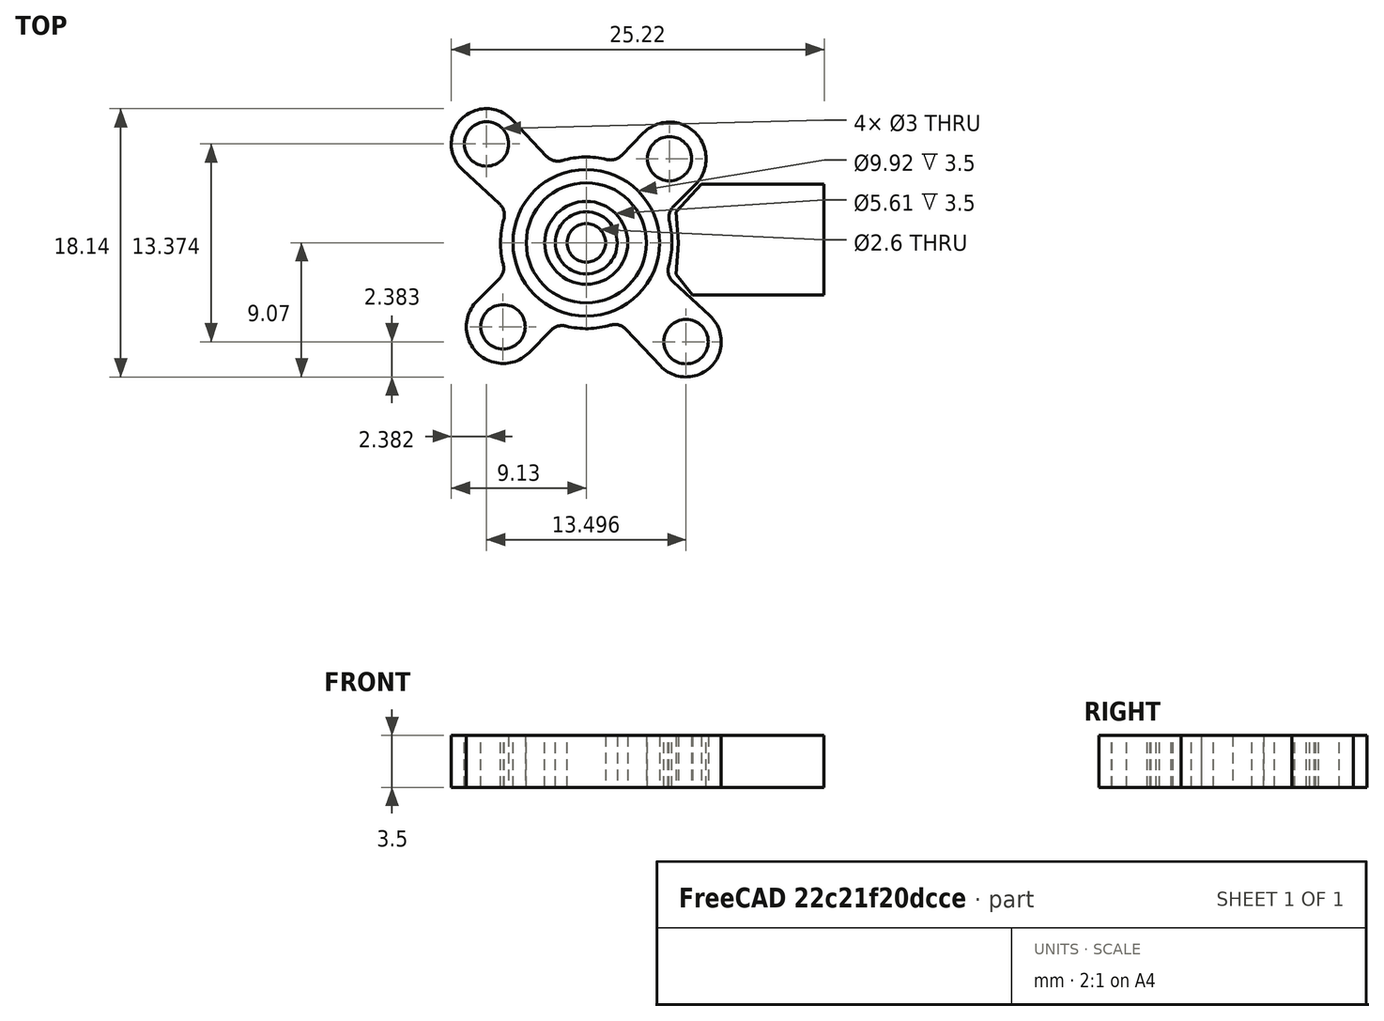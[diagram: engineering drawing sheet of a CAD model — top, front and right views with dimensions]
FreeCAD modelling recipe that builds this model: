
FCSTD DOCUMENT  (FreeCAD 0.18RUnknown)
Label: r6
License: All rights reserved
LicenseURL: http://en.wikipedia.org/wiki/All_rights_reserved
objects: Sketcher::SketchObject×2, Image::ImagePlane×2, Part::Revolution×1, Part::Extrusion×1, App::Part×1
note: 4 computed .brp shape members not serialized (recipe doc carries the construction recipe); baked Part::Feature solids carry a one-line shape summary decoded from their .brp

FEATURE [Sketcher::SketchObject] Sketch  label="body"
  Placement = pos=(0,0,0) rot=(1,0,0;1.5708rad)
  sketch-geometry (23):
    g0: LineSegment StartX=-14 StartY=0 StartZ=0 EndX=14 EndY=0 EndZ=0
    g1: LineSegment StartX=14 StartY=0 StartZ=0 EndX=14 EndY=7.7 EndZ=0
    g2: LineSegment StartX=14 StartY=7.7 StartZ=0 EndX=-14 EndY=7.7 EndZ=0
    g3: LineSegment StartX=-14 StartY=0 StartZ=0 EndX=-14 EndY=7.7 EndZ=0
    g4: LineSegment StartX=-5.833 StartY=13.25 StartZ=0 EndX=5.833 EndY=13.25 EndZ=0
    g5: LineSegment StartX=-2.5 StartY=13.25 StartZ=0 EndX=-2.5 EndY=18.25 EndZ=0
    g6: LineSegment StartX=-2.5 StartY=18.25 StartZ=0 EndX=2.5 EndY=18.25 EndZ=0
    g7: LineSegment StartX=2.5 StartY=18.25 StartZ=0 EndX=2.5 EndY=13.25 EndZ=0
    g8: LineSegment StartX=-2.5 StartY=18.25 StartZ=0 EndX=-2.5 EndY=25.25 EndZ=0
    g9: LineSegment StartX=-2.5 StartY=25.25 StartZ=0 EndX=2.5 EndY=25.25 EndZ=0
    g10: LineSegment StartX=2.5 StartY=25.25 StartZ=0 EndX=2.5 EndY=18.25 EndZ=0
    g11: LineSegment StartX=-5.175 StartY=0 StartZ=0 EndX=-5.75 EndY=-2 EndZ=0
    g12: LineSegment StartX=5.175 StartY=0 StartZ=0 EndX=5.75 EndY=-2 EndZ=0
    g13: LineSegment StartX=-5.75 StartY=-2 StartZ=0 EndX=5.75 EndY=-2 EndZ=0
    g14: GeomPoint X=0 Y=-5.45 Z=0
    g15: GeomPoint X=0 Y=25.25 Z=0
    g16: GeomPoint X=0 Y=13.25 Z=0
    g17: GeomPoint X=10.0114 Y=8.91857 Z=0
    g18: LineSegment StartX=14 StartY=7.7 StartZ=0 EndX=14 EndY=9.64 EndZ=0
    g19: LineSegment StartX=14 StartY=9.64 StartZ=0 EndX=5.833 EndY=13.25 EndZ=0
    g20: LineSegment StartX=-5.833 StartY=13.25 StartZ=0 EndX=-14 EndY=9.64 EndZ=0
    g21: LineSegment StartX=-14 StartY=7.7 StartZ=0 EndX=-14 EndY=9.64 EndZ=0
    g22: GeomPoint X=0 Y=7.7 Z=0
  constraints (62):
    c: PointOnObject(g0,g-1)
    c: Horizontal(g0)
    c: Vertical(g1)
    c: Horizontal(g2)
    c: Coincident(g3,g0)
    c: Coincident(g3,g2)
    c: Vertical(g3)
    c: Horizontal(g4)
    c: PointOnObject(g5,g4)
    c: Vertical(g5)
    c: Coincident(g6,g5)
    c: Horizontal(g6)
    c: Coincident(g7,g6)
    c: PointOnObject(g7,g4)
    c: Vertical(g7)
    c: Coincident(g8,g5)
    c: Vertical(g8)
    c: Horizontal(g9)
    c: Coincident(g10,g9)
    c: Coincident(g10,g6)
    c: Vertical(g10)
    c: PointOnObject(g11,g0)
    c: PointOnObject(g12,g0)
    c: Coincident(g13,g11)
    c: Horizontal(g13)
    c: Coincident(g12,g13)
    c: Coincident(g2,g1)
    c: DistanceY(g11,g11) = 2
    c: PointOnObject(g14,g-2)
    c: Equal(g11,g12)
    c: PointOnObject(g15,g9)
    c: PointOnObject(g16,g4)
    c: PointOnObject(g16,g-2)
    c: PointOnObject(g15,g-2)
    c: Coincident(g9,g8)
    c: DistanceY(g14,g16) = 18.7
    c: Coincident(g0,g1)
    c: DistanceY(g14,g15) = 30.7
    c: DistanceX(g8,g9) = 5
    c: DistanceY(g5,g8) = 7
    c: Symmetric(g8,g9,g-2)
    c: Symmetric(g4,g4,g-2)
    c: DistanceX(g2,g1) = 28
    c: Symmetric(g2,g1,g-2)
    c: DistanceY(g0,g1) = 7.7
    c: Coincident(g18,g1)
    c: Coincident(g19,g18)
    c: Coincident(g19,g4)
    c: Coincident(g20,g4)
    c: Coincident(g21,g2)
    c: Coincident(g21,g20)
    c: Vertical(g18)
    c: Equal(g18,g21)
    c: Equal(g19,g20)
    c: PointOnObject(g22,g2)
    c: PointOnObject(g22,g-2)
    c: DistanceY(g22,g16) = 5.55
    c: Symmetric(g11,g12,g-2)
    c: DistanceX(g11,g12) = 10.35
    c: DistanceY(g1,g18) = 1.94
    c: DistanceX(g11,g12) = 11.5
    c: DistanceX(g4,g4) = 11.666
FEATURE [Image::ImagePlane] ImagePlane
  Placement = pos=(21.6,7,10.67) rot=(-1,0,0;4.71239rad)
  XSize = 114
  YSize = 114
FEATURE [Part::Revolution] Revolve
  Angle = 360
  Axis = (0,0,1)
  Base = (0,0,0)
  FaceMakerClass = Part::FaceMakerBullseye
  Placement = pos=(0,0,5.5) rot=(0,0,1;0rad)
  Solid = false
  Source = -> Sketch
  Symmetric = false
FEATURE [Image::ImagePlane] ImagePlane001
  Placement = pos=(21.7,-40.3,-1.33) rot=(-1,0,0;0rad)
  XSize = 114
  YSize = 114
FEATURE [Sketcher::SketchObject] Sketch001  label="base"
  sketch-geometry (51):
    g0: Circle CenterX=0 CenterY=0 CenterZ=0 NormalX=0 NormalY=0 NormalZ=1 AngleXU=0 Radius=4.95833
    g1: Circle CenterX=0 CenterY=0 CenterZ=0 NormalX=0 NormalY=0 NormalZ=1 AngleXU=0 Radius=4.05855
    g2: Circle CenterX=0 CenterY=0 CenterZ=0 NormalX=0 NormalY=0 NormalZ=1 AngleXU=0 Radius=2.80253
    g3: Circle CenterX=0 CenterY=0 CenterZ=0 NormalX=0 NormalY=0 NormalZ=1 AngleXU=0 Radius=2.09587
    g4: Circle CenterX=0 CenterY=0 CenterZ=0 NormalX=0 NormalY=0 NormalZ=1 AngleXU=0 Radius=1.30129
    g5: ArcOfCircle CenterX=6.748 CenterY=6.68689 CenterZ=0 NormalX=0 NormalY=0 NormalZ=1 AngleXU=0 Radius=2.38428 StartAngle=5.45879 EndAngle=8.66928
    g6: ArcOfCircle CenterX=5.63107 CenterY=-5.68252 CenterZ=0 NormalX=0 NormalY=0 NormalZ=1 AngleXU=0 Radius=2.47766 StartAngle=3.91796 EndAngle=7.06852
    g7: ArcOfCircle CenterX=-6.748 CenterY=-6.68689 CenterZ=0 NormalX=0 NormalY=0 NormalZ=1 AngleXU=0 Radius=2.38428 StartAngle=2.3172 EndAngle=5.52769
    g8: ArcOfCircle CenterX=-5.63107 CenterY=5.68252 CenterZ=0 NormalX=0 NormalY=0 NormalZ=1 AngleXU=0 Radius=2.47766 StartAngle=0.776367 EndAngle=3.92693
    g9: ArcOfCircle CenterX=0 CenterY=0 CenterZ=0 NormalX=0 NormalY=0 NormalZ=1 AngleXU=0 Radius=5.8 StartAngle=1.28437 EndAngle=1.81386
    g10: ArcOfCircle CenterX=0 CenterY=0 CenterZ=0 NormalX=0 NormalY=0 NormalZ=1 AngleXU=0 Radius=5.8 StartAngle=6.03102 EndAngle=6.56052
    g11: ArcOfCircle CenterX=0 CenterY=0 CenterZ=0 NormalX=0 NormalY=0 NormalZ=1 AngleXU=0 Radius=5.8 StartAngle=2.88943 EndAngle=3.41892
    g12: ArcOfCircle CenterX=0 CenterY=0 CenterZ=0 NormalX=0 NormalY=0 NormalZ=1 AngleXU=0 Radius=5.8 StartAngle=4.42596 EndAngle=4.95546
    g13: ArcOfCircle CenterX=-1.9299 CenterY=-6.55258 CenterZ=0 NormalX=0 NormalY=0 NormalZ=1 AngleXU=0 Radius=1.03087 StartAngle=1.28437 EndAngle=2.3861
    g14: LineSegment StartX=-2.6803 StartY=-5.84576 StartZ=0 EndX=-5.0124 EndY=-8.32168 EndZ=0
    g15: ArcOfCircle CenterX=1.9299 CenterY=6.55258 CenterZ=0 NormalX=0 NormalY=0 NormalZ=1 AngleXU=0 Radius=1.03087 StartAngle=4.42596 EndAngle=5.52769
    g16: ArcOfCircle CenterX=6.56986 CenterY=1.87022 CenterZ=0 NormalX=0 NormalY=0 NormalZ=1 AngleXU=0 Radius=1.03087 StartAngle=2.3172 EndAngle=3.41892
    g17: ArcOfCircle CenterX=6.61484 CenterY=-1.70429 CenterZ=0 NormalX=0 NormalY=0 NormalZ=1 AngleXU=0 Radius=1.03087 StartAngle=2.88943 EndAngle=3.92693
    g18: ArcOfCircle CenterX=1.64406 CenterY=-6.63007 CenterZ=0 NormalX=0 NormalY=0 NormalZ=1 AngleXU=0 Radius=1.03087 StartAngle=0.776367 EndAngle=1.81386
    g19: ArcOfCircle CenterX=-6.56986 CenterY=-1.87022 CenterZ=0 NormalX=0 NormalY=0 NormalZ=1 AngleXU=0 Radius=1.03087 StartAngle=5.45879 EndAngle=6.56052
    g20: ArcOfCircle CenterX=-6.61484 CenterY=1.70429 CenterZ=0 NormalX=0 NormalY=0 NormalZ=1 AngleXU=0 Radius=1.03087 StartAngle=6.03102 EndAngle=7.06852
    g21: ArcOfCircle CenterX=-1.64406 CenterY=6.63007 CenterZ=0 NormalX=0 NormalY=0 NormalZ=1 AngleXU=0 Radius=1.03087 StartAngle=3.91796 EndAngle=4.95546
    g22: LineSegment StartX=-3.86335 StartY=7.4186 StartZ=0 EndX=-2.37954 EndY=5.90775 EndZ=0
    g23: LineSegment StartX=-5.88586 StartY=2.43318 StartZ=0 EndX=-7.38315 EndY=3.93067 EndZ=0
    g24: LineSegment StartX=-5.8699 StartY=-2.62702 StartZ=0 EndX=-8.36692 EndY=-4.93651 EndZ=0
    g25: LineSegment StartX=2.37954 StartY=-5.90775 StartZ=0 EndX=3.86335 EndY=-7.4186 EndZ=0
    g26: LineSegment StartX=7.38315 StartY=-3.93067 StartZ=0 EndX=5.88586 EndY=-2.43318 EndZ=0
    g27: LineSegment StartX=5.8699 StartY=2.62702 StartZ=0 EndX=8.36692 EndY=4.93651 EndZ=0
    g28: LineSegment StartX=2.6803 StartY=5.84576 StartZ=0 EndX=5.0124 EndY=8.32168 EndZ=0
    g29: Circle [constr] CenterX=0 CenterY=0 CenterZ=0 NormalX=0 NormalY=0 NormalZ=1 AngleXU=0 Radius=8
    g30: Circle [constr] CenterX=0 CenterY=0 CenterZ=0 NormalX=0 NormalY=0 NormalZ=1 AngleXU=0 Radius=9.5
    g31: Circle [constr] CenterX=0 CenterY=0 CenterZ=0 NormalX=0 NormalY=0 NormalZ=1 AngleXU=0 Radius=5.8
    g32: LineSegment [constr] StartX=-6.748 StartY=-6.68689 StartZ=0 EndX=6.748 EndY=6.68689 EndZ=0
    g33: LineSegment [constr] StartX=-5.63107 StartY=5.68252 StartZ=0 EndX=5.63107 EndY=-5.68252 EndZ=0
    g34: Circle CenterX=6.748 CenterY=6.68689 CenterZ=0 NormalX=0 NormalY=0 NormalZ=1 AngleXU=0 Radius=1.5
    g35: Circle CenterX=-5.63107 CenterY=5.68252 CenterZ=0 NormalX=0 NormalY=0 NormalZ=1 AngleXU=0 Radius=1.5
    g36: Circle CenterX=-6.748 CenterY=-6.68689 CenterZ=0 NormalX=0 NormalY=0 NormalZ=1 AngleXU=0 Radius=1.5
    g37: Circle CenterX=5.63107 CenterY=-5.68252 CenterZ=0 NormalX=0 NormalY=0 NormalZ=1 AngleXU=0 Radius=1.5
    g38: LineSegment StartX=16.0881 StartY=-3.97669 StartZ=0 EndX=16.0881 EndY=3.52014 EndZ=0
    g39: GeomPoint X=16.0952 Y=3.53033 Z=0
    g40: GeomPoint X=16.0881 Y=3.52014 Z=0
    g41: GeomPoint X=16.0952 Y=3.53033 Z=0
    g42: GeomPoint X=16.0881 Y=3.52014 Z=0
    g43: GeomPoint X=16.0952 Y=3.53033 Z=0
    g44: GeomPoint X=12.9914 Y=0 Z=0
    g45: LineSegment StartX=16.0881 StartY=3.52014 StartZ=0 EndX=7.18391 EndY=3.52014 EndZ=0
    g46: LineSegment StartX=7.18391 StartY=3.52014 StartZ=0 EndX=6.0724 EndY=2.14391 EndZ=0
    g47: LineSegment StartX=6.0724 StartY=2.14391 StartZ=0 EndX=6.22587 EndY=0 EndZ=0
    g48: LineSegment StartX=6.22587 StartY=0 StartZ=0 EndX=6.06438 EndY=-2.09343 EndZ=0
    g49: LineSegment StartX=6.06438 StartY=-2.09343 StartZ=0 EndX=7.79416 EndY=-3.97669 EndZ=0
    g50: LineSegment StartX=7.79416 StartY=-3.97669 StartZ=0 EndX=16.0881 EndY=-3.97669 EndZ=0
  constraints (114):
    c: Coincident(g0,g-1)
    c: Coincident(g2,g-1)
    c: Coincident(g3,g-1)
    c: Coincident(g4,g-1)
    c: Tangent(g14,g13) = -1.5708
    c: Tangent(g13,g12) = 1.5708
    c: Tangent(g14,g7) = 1.5708
    c: Coincident(g15,g9)
    c: Coincident(g16,g10)
    c: Coincident(g17,g10)
    c: Coincident(g18,g12)
    c: Coincident(g19,g11)
    c: Coincident(g20,g11)
    c: Coincident(g21,g9)
    c: Coincident(g22,g8)
    c: Coincident(g22,g21)
    c: Coincident(g23,g20)
    c: Coincident(g23,g8)
    c: Coincident(g24,g19)
    c: Coincident(g24,g7)
    c: Coincident(g25,g18)
    c: Coincident(g25,g6)
    c: Coincident(g26,g6)
    c: Coincident(g26,g17)
    c: Coincident(g27,g16)
    c: Coincident(g27,g5)
    c: Coincident(g28,g15)
    c: Coincident(g28,g5)
    c: Tangent(g28,g15)
    c: Tangent(g9,g15)
    c: Tangent(g28,g5)
    c: Tangent(g5,g27)
    c: Tangent(g16,g27)
    c: Tangent(g16,g10)
    c: Tangent(g10,g17)
    c: Tangent(g17,g26)
    c: Tangent(g26,g6)
    c: Tangent(g6,g25)
    c: Tangent(g25,g18)
    c: Tangent(g12,g18)
    c: Tangent(g7,g24)
    c: Tangent(g24,g19)
    c: Tangent(g19,g11)
    c: Tangent(g11,g20)
    c: Tangent(g20,g23)
    c: Tangent(g23,g8)
    c: Tangent(g22,g8)
    c: Tangent(g22,g21)
    c: Tangent(g9,g21)
    c: Coincident(g29,g-1)
    c: Coincident(g30,g-1)
    c: PointOnObject(g8,g29)
    c: PointOnObject(g5,g30)
    c: PointOnObject(g6,g29)
    c: PointOnObject(g7,g30)
    c: Coincident(g31,g-1)
    c: PointOnObject(g9,g31)
    c: PointOnObject(g9,g31)
    c: Radius(g29) = 8
    c: Radius(g30) = 9.5
    c: Radius(g31) = 5.8
    c: PointOnObject(g10,g31)
    c: PointOnObject(g12,g31)
    c: PointOnObject(g12,g31)
    c: PointOnObject(g10,g31)
    c: PointOnObject(g11,g31)
    c: PointOnObject(g11,g31)
    c: Equal(g5,g7)
    c: Equal(g8,g6)
    c: Equal(g13,g18)
    c: Equal(g13,g19)
    c: Equal(g20,g19)
    c: Equal(g21,g15)
    c: Equal(g21,g20)
    c: Equal(g15,g16)
    c: Equal(g17,g16)
    c: Equal(g11,g12)
    c: Equal(g12,g10)
    c: Equal(g10,g9)
    c: Equal(g22,g23)
    c: Equal(g22,g26)
    c: Equal(g26,g25)
    c: Equal(g14,g24)
    c: Equal(g28,g27)
    c: Equal(g28,g24)
    c: Coincident(g32,g7)
    c: PointOnObject(g-1,g32)
    c: Coincident(g1,g-1)
    c: PointOnObject(g10,g32)
    c: Coincident(g32,g5)
    c: Coincident(g33,g8)
    c: Coincident(g33,g6)
    c: Angle(g33,g32) = 1.5708
    c: Coincident(g34,g5)
    c: Radius(g34) = 1.5
    c: Coincident(g35,g8)
    c: Coincident(g36,g7)
    c: Coincident(g37,g6)
    c: Equal(g34,g35)
    c: Equal(g35,g36)
    c: Equal(g36,g37)
    c: PointOnObject(g-1,g33)
    c: Vertical(g38)
    c: Coincident(g40,g38)
    c: Coincident(g42,g38)
    c: Coincident(g45,g38)
    c: Horizontal(g45)
    c: Coincident(g47,g46)
    c: Coincident(g48,g47)
    c: Coincident(g49,g48)
    c: Coincident(g50,g38)
    c: Horizontal(g50)
    c: Coincident(g50,g49)
    c: Coincident(g46,g45)
FEATURE [Part::Extrusion] Extrude
  Base = -> Sketch001
  Dir = (0,0,1)
  DirMode = 2
  FaceMakerClass = Part::FaceMakerBullseye
  LengthFwd = 3.5
  LengthRev = 0
  Placement = pos=(0,0,0) rot=(1,0,0;3.14159rad)
  Solid = true
  Symmetric = false
FEATURE [App::Part] Part001  label="R6 motor"
  Group = -> [Sketch001,Extrude,Sketch,Revolve,ImagePlane001,ImagePlane]
  License = CC BY 3.0
  LicenseURL = http://creativecommons.org/licenses/by/3.0/
  Origin = -> Origin001
